# Revit family: Saxi Teanik 2000
name_source: partatom
category: Mechanical Equipment
revit_build: Autodesk Revit Architecture 2015 (Build: 20140322_1515(x64)
units: mm (PartAtom-declared; Revit-internal decimal feet)

## types (1)
- Standard
    BRACKETS_ARRAY_VISIBLE = Yes
    BRACKETS_SINGLE_VISIBLE = No
    Bearing_Offset = 8105 mm  [stored 26.5912 ft]
    Bracket_Offset = 3000 mm  [stored 9.84252 ft]
    Center = 11000 mm  [stored 36.0892 ft]
    Description = Saxi Curtain wall
    Design Status = 1
    DukHöjdUpphissad = 650 mm  [stored 2.13255 ft]
    Dukbredd = 21950 mm  [stored 72.0144 ft]
    FirstHelvadVisibleARRAY = Yes
    FirstHelvadVisibleSINGLE = No
    First_Bracket = 9650 mm  [stored 31.6601 ft]
    Height = 7950 mm  [stored 26.0827 ft]
    Height_floor_to_toppvad = 7592 mm  [stored 24.9081 ft]
    HelvadOffset = 2650 mm  [stored 8.69423 ft]
    Manufacturer = Saxi Vägg AB
    Massa_per_m2 = 6.00 kg/m²
    Model = Saxi Teanik 2000
    MotorHeightOffset = 8118 mm  [stored 26.6339 ft]
    Motorplacement = 10940 mm
    NO_BRACKETS_REAL = 3
    No_Helvader = 2
    No_Helvader_REAL = 2
    Part Number = Saxi Teanik 2000
    Shaft offset = 8105 mm  [stored 26.5912 ft]
    Shaft_LENGTH = 21400 mm
    Toppvåd_Height = 200 mm  [stored 0.656168 ft]
    Toppvåd_Height_REAL = 200 mm  [stored 0.656168 ft]
    Type Comments = Standard, speciallösningar utföres på förfrågan
    URL = http://www.saxi.se
    Weight = 1049.40 kg
    Width = 22000 mm  [stored 72.1785 ft]
    d25 = 2400 mm
    d27 = 2400 mm
    d29 = 2400 mm
    d31 = 2400 mm
    d33 = 2400 mm
    höjdljudfälla = 2400 mm

note: [stored X ft] marks values corroborated as IEEE doubles in the binary element streams (Revit-internal decimal feet)

## geometry (parser evidence)
native form markers: Sweep x23
no freeform markers — native parametric forms only
